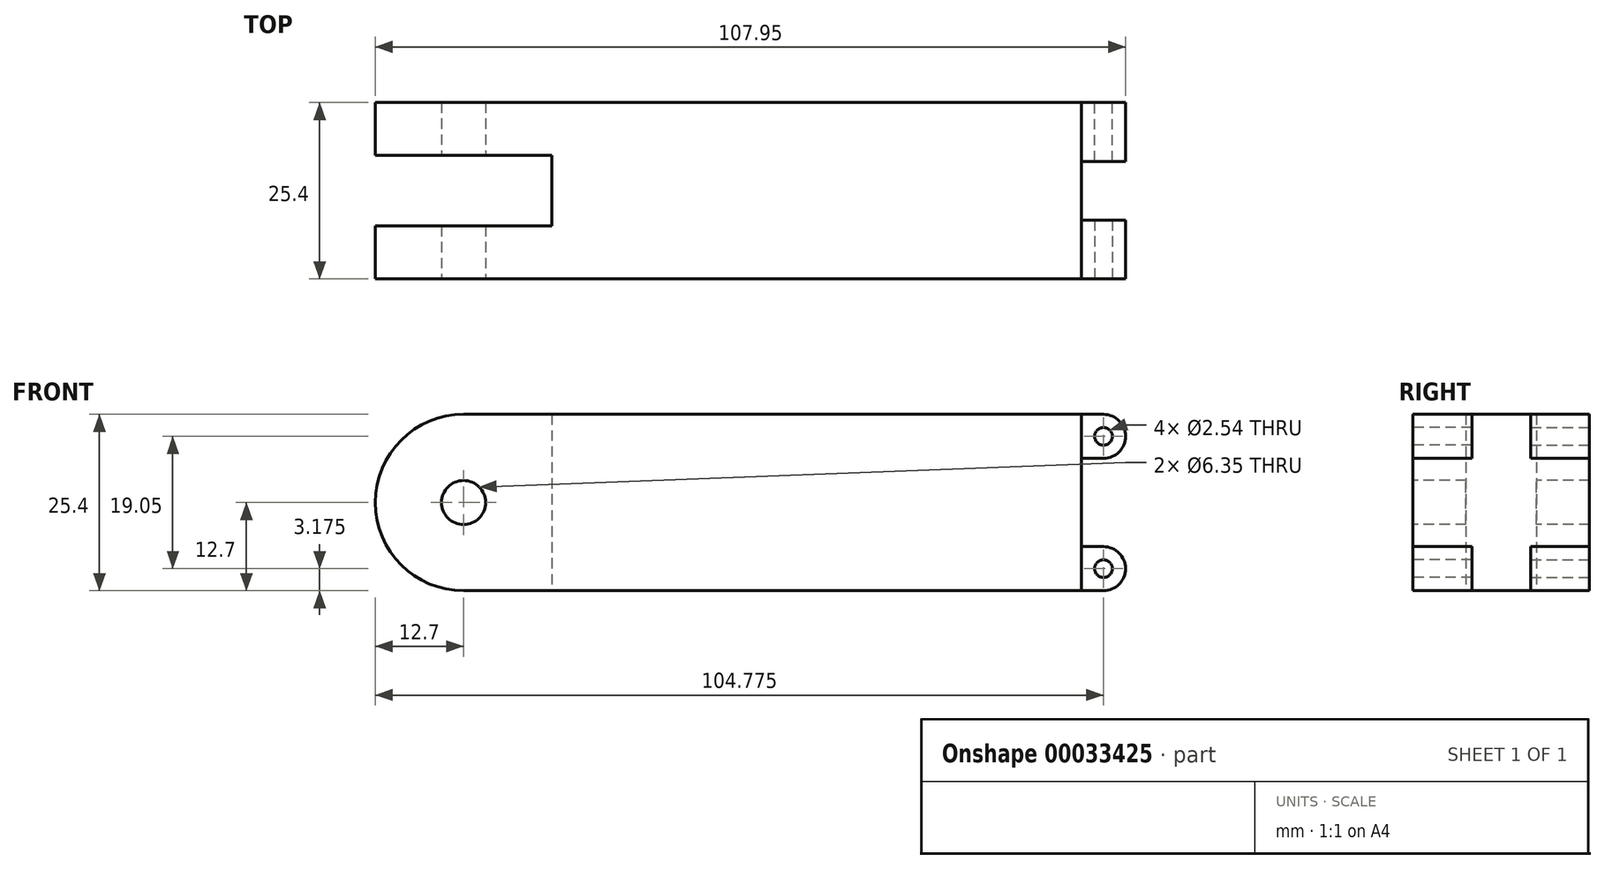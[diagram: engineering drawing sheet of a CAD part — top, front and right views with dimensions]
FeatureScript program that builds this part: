
annotation { "Feature Type Name" : "Feature", "Feature Type Description" : "" }
export const myFeature = defineFeature(function(context is Context, id is Id, definition is map)
    precondition{}
    {
        {
            var Q0;
            Q0=qCreatedBy(makeId("Front.planeOp"),FACE);
            var sketch = newSketch(context, id + "F0", { "sketchPlane" : qUnion([Q0])});
            skLineSegment(sketch, "E0.rect.bottom", {"start": v(-38.1, 12.7) * mm, "end": v(38.1, 12.7) * mm});
            skLineSegment(sketch, "E0.rect.top", {"start": v(-38.1, -12.7) * mm, "end": v(38.1, -12.7) * mm});
            skLineSegment(sketch, "E0.rect.left", {"start": v(-38.1, 12.7) * mm, "end": v(-38.1, -12.7) * mm});
            skLineSegment(sketch, "E0.rect.right", {"start": v(38.1, 12.7) * mm, "end": v(38.1, -12.7) * mm});
            skPoint(sketch, "E0.rect.middle", {"position": v(0, 0) * mm});
            skSolve(sketch);
        }
        {
            var Q0;
            Q0 = qSketchRegion(id + "F0", true);
            extrude(context, id + "F1", {"entities" : qUnion([Q0]), "depth" : 25.4 * mm});
        }
        {
            var Q0;
            Q0=makeQuery(id+"F1.opExtrude","SWEPT_FACE",FACE,{"disambiguationData":[OSD([sQuery(id+"F0.wireOp",EDGE,"E0.rect.left")])]});
            var sketch = newSketch(context, id + "F2", { "sketchPlane" : qUnion([Q0])});
            skLineSegment(sketch, "E1.bottom", {"start": v(0, 12.7) * mm, "end": v(7.62, 12.7) * mm});
            skLineSegment(sketch, "E1.top", {"start": v(0, -12.7) * mm, "end": v(7.62, -12.7) * mm});
            skLineSegment(sketch, "E1.left", {"start": v(0, 12.7) * mm, "end": v(0, -12.7) * mm});
            skLineSegment(sketch, "E1.right", {"start": v(7.62, 12.7) * mm, "end": v(7.62, -12.7) * mm});
            skLineSegment(sketch, "E2.bottom", {"start": v(25.4, 12.7) * mm, "end": v(17.78, 12.7) * mm});
            skLineSegment(sketch, "E2.top", {"start": v(25.4, -12.7) * mm, "end": v(17.78, -12.7) * mm});
            skLineSegment(sketch, "E2.left", {"start": v(25.4, 12.7) * mm, "end": v(25.4, -12.7) * mm});
            skLineSegment(sketch, "E2.right", {"start": v(17.78, 12.7) * mm, "end": v(17.78, -12.7) * mm});
            skSolve(sketch);
        }
        {
            var Q0;
            Q0 = qSketchRegion(id + "F2", true);
            extrude(context, id + "F3", {"entities" : qUnion([Q0]), "operationType" : NewBodyOperationType.ADD, "depth" : 25.4 * mm});
        }
        {
            var Q0;
            Q0=makeQuery(id+"F3.boolean.opBoolean","MERGE",FACE,{"derivedFrom":[makeQuery(id+"F1.opExtrude","CAP_FACE",FACE,{"disambiguationData":[OSD([sQuery(id+"F0.wireOp",EDGE,"E0.rect.bottom"),sQuery(id+"F0.wireOp",EDGE,"E0.rect.top"),sQuery(id+"F0.wireOp",EDGE,"E0.rect.left"),sQuery(id+"F0.wireOp",EDGE,"E0.rect.right")])],"isStart":false}),makeQuery(id+"F3.opExtrude","SWEPT_FACE",FACE,{"disambiguationData":[OSD([sQuery(id+"F2.wireOp",EDGE,"E2.left")])]})]});
            var sketch = newSketch(context, id + "F4", { "sketchPlane" : qUnion([Q0])});
            skLineSegment(sketch, "E3.bottom", {"start": v(-63.5, 12.7) * mm, "end": v(-38.1, 12.7) * mm});
            skLineSegment(sketch, "E3.top", {"start": v(-63.5, -12.7) * mm, "end": v(-38.1, -12.7) * mm});
            skLineSegment(sketch, "E3.left", {"start": v(-63.5, 12.7) * mm, "end": v(-63.5, -12.7) * mm});
            skLineSegment(sketch, "E3.right", {"start": v(-38.1, 12.7) * mm, "end": v(-38.1, -12.7) * mm});
            skCircle(sketch, "E4", {"center": v(-50.8, 0) * mm, "radius": 12.7 * mm});
            skPoint(sketch, "E4.first.point", {"position": v(-50.8, 12.7) * mm});
            skPoint(sketch, "E4.second.point", {"position": v(-38.1, 0) * mm});
            skPoint(sketch, "E4.third.point", {"position": v(-50.8, -12.7) * mm});
            skCircle(sketch, "E5", {"center": v(-50.8, 0) * mm, "radius": 3.18 * mm});
            skSolve(sketch);
        }
        {
            var Q0;
            {var subQ1=sQuery(id+"F4.wireOp",EDGE,"E3.left");var subQ3=sQuery(id+"F4.wireOp",EDGE,"E3.bottom");var subQ5=makeQuery(id+"F4.imprint","INTERSECT",VERTEX,{"derivedFrom":[subQ3,subQ1]});Q0=makeQuery(id+"F4.imprint","IMPRINT",FACE,{"disambiguationData":[TD([[makeQuery(id+"F4.imprint","IMPRINT",EDGE,{"disambiguationData":[TD([[subQ5,-1.0]])],"derivedFrom":subQ3}),-1.0]])]});}
            var Q1;
            {var subQ1=sQuery(id+"F4.wireOp",EDGE,"E3.left");var subQ3=sQuery(id+"F4.wireOp",EDGE,"E3.top");var subQ5=makeQuery(id+"F4.imprint","INTERSECT",VERTEX,{"derivedFrom":[subQ3,subQ1]});Q1=makeQuery(id+"F4.imprint","IMPRINT",FACE,{"disambiguationData":[TD([[makeQuery(id+"F4.imprint","IMPRINT",EDGE,{"disambiguationData":[TD([[subQ5,-1.0]])],"derivedFrom":subQ3}),1.0]])]});}
            var Q2;
            Q2=makeQuery(id+"F4.imprint","IMPRINT",FACE,{"disambiguationData":[TD([[makeQuery(id+"F4.imprint","IMPRINT",EDGE,{"derivedFrom":sQuery(id+"F4.wireOp",EDGE,"E5")}),1.0]])]});
            extrude(context, id + "F5", {"entities" : qUnion([Q0, Q1, Q2]), "operationType" : NewBodyOperationType.REMOVE, "oppositeDirection" : true, "depth" : 25.4 * mm});
        }
        {
            var Q0;
            Q0=makeQuery(id+"F3.boolean.opBoolean","MERGE",FACE,{"derivedFrom":[makeQuery(id+"F1.opExtrude","CAP_FACE",FACE,{"disambiguationData":[OSD([sQuery(id+"F0.wireOp",EDGE,"E0.rect.bottom"),sQuery(id+"F0.wireOp",EDGE,"E0.rect.top"),sQuery(id+"F0.wireOp",EDGE,"E0.rect.left"),sQuery(id+"F0.wireOp",EDGE,"E0.rect.right")])],"isStart":false}),makeQuery(id+"F3.opExtrude","SWEPT_FACE",FACE,{"disambiguationData":[OSD([sQuery(id+"F2.wireOp",EDGE,"E2.left")])]})]});
            var sketch = newSketch(context, id + "F6", { "sketchPlane" : qUnion([Q0])});
            skLineSegment(sketch, "E6.bottom", {"start": v(38.1, -12.7) * mm, "end": v(41.27, -12.7) * mm});
            skLineSegment(sketch, "E6.top", {"start": v(38.1, -6.35) * mm, "end": v(41.27, -6.35) * mm});
            skLineSegment(sketch, "E6.left", {"start": v(38.1, -12.7) * mm, "end": v(38.1, -6.35) * mm});
            skLineSegment(sketch, "E6.right", {"start": v(41.27, -12.7) * mm, "end": v(41.27, -6.35) * mm});
            skLineSegment(sketch, "E7.bottom", {"start": v(38.1, 12.7) * mm, "end": v(41.27, 12.7) * mm});
            skLineSegment(sketch, "E7.top", {"start": v(38.1, 6.35) * mm, "end": v(41.27, 6.35) * mm});
            skLineSegment(sketch, "E7.left", {"start": v(38.1, 12.7) * mm, "end": v(38.1, 6.35) * mm});
            skLineSegment(sketch, "E7.right", {"start": v(41.27, 12.7) * mm, "end": v(41.27, 6.35) * mm});
            skCircle(sketch, "E8", {"center": v(41.27, -9.52) * mm, "radius": 3.17 * mm});
            skCircle(sketch, "E9", {"center": v(41.27, 9.53) * mm, "radius": 3.18 * mm});
            skCircle(sketch, "E10", {"center": v(41.27, -9.52) * mm, "radius": 1.27 * mm});
            skCircle(sketch, "E11", {"center": v(41.27, 9.53) * mm, "radius": 1.27 * mm});
            skSolve(sketch);
        }
        {
            var Q0;
            Q0 = qSketchRegion(id + "F6", true);
            extrude(context, id + "F7", {"entities" : qUnion([Q0]), "oppositeDirection" : true, "depth" : 8.47 * mm});
        }
        {
            var Q0;
            Q0=makeQuery(id+"F3.boolean.opBoolean","MERGE",FACE,{"derivedFrom":[makeQuery(id+"F1.opExtrude","CAP_FACE",FACE,{"disambiguationData":[OSD([sQuery(id+"F0.wireOp",EDGE,"E0.rect.bottom"),sQuery(id+"F0.wireOp",EDGE,"E0.rect.top"),sQuery(id+"F0.wireOp",EDGE,"E0.rect.left"),sQuery(id+"F0.wireOp",EDGE,"E0.rect.right")])],"isStart":true}),makeQuery(id+"F3.opExtrude","SWEPT_FACE",FACE,{"disambiguationData":[OSD([sQuery(id+"F2.wireOp",EDGE,"E1.left")])]})]});
            var sketch = newSketch(context, id + "F8", { "sketchPlane" : qUnion([Q0])});
            skLineSegment(sketch, "E12.bottom", {"start": v(-38.1, -12.7) * mm, "end": v(-41.27, -12.7) * mm});
            skLineSegment(sketch, "E12.top", {"start": v(-38.1, -6.35) * mm, "end": v(-41.27, -6.35) * mm});
            skLineSegment(sketch, "E12.left", {"start": v(-38.1, -12.7) * mm, "end": v(-38.1, -6.35) * mm});
            skLineSegment(sketch, "E12.right", {"start": v(-41.27, -12.7) * mm, "end": v(-41.27, -6.35) * mm});
            skLineSegment(sketch, "E13.bottom", {"start": v(-38.1, 12.7) * mm, "end": v(-41.27, 12.7) * mm});
            skLineSegment(sketch, "E13.top", {"start": v(-38.1, 6.35) * mm, "end": v(-41.27, 6.35) * mm});
            skLineSegment(sketch, "E13.left", {"start": v(-38.1, 12.7) * mm, "end": v(-38.1, 6.35) * mm});
            skLineSegment(sketch, "E13.right", {"start": v(-41.27, 12.7) * mm, "end": v(-41.27, 6.35) * mm});
            skCircle(sketch, "E14", {"center": v(-41.27, -9.52) * mm, "radius": 3.17 * mm});
            skCircle(sketch, "E15", {"center": v(-41.27, 9.53) * mm, "radius": 3.17 * mm});
            skCircle(sketch, "E16", {"center": v(-41.27, -9.52) * mm, "radius": 1.27 * mm});
            skCircle(sketch, "E17", {"center": v(-41.27, 9.53) * mm, "radius": 1.27 * mm});
            skSolve(sketch);
        }
        {
            var Q0;
            Q0 = qSketchRegion(id + "F8", true);
            extrude(context, id + "F9", {"entities" : qUnion([Q0]), "oppositeDirection" : true, "depth" : 8.47 * mm});
        }
    });
